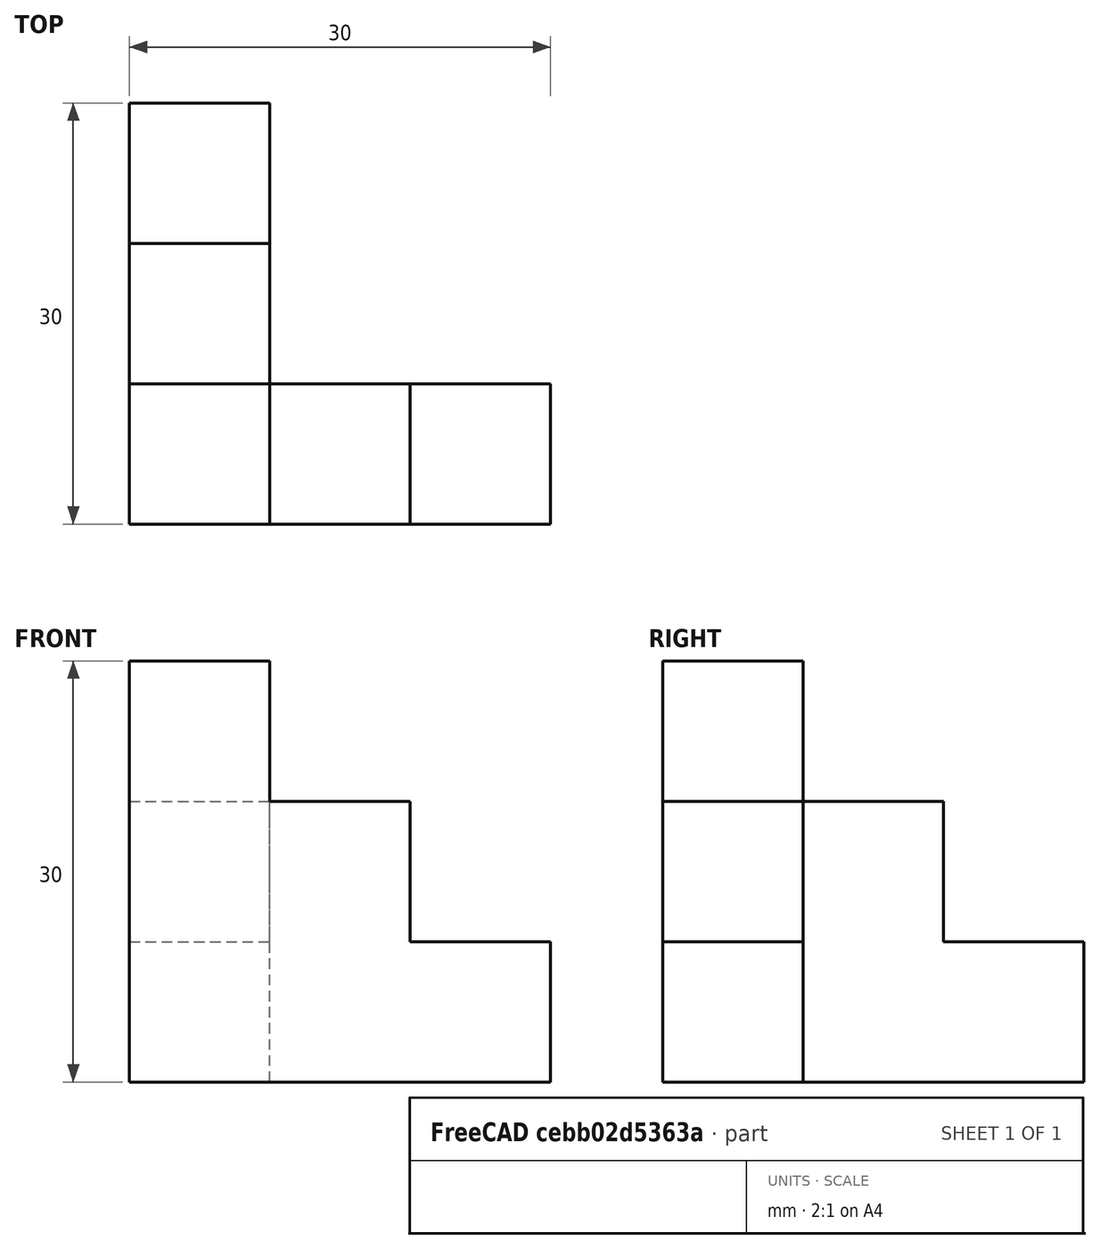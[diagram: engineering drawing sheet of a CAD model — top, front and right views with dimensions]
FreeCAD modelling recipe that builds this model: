
FCSTD DOCUMENT  (FreeCAD 0.21R33771 (Git))
Label: OJT1_T05R02_unions_qubert3_v2
License: All rights reserved
LicenseURL: http://en.wikipedia.org/wiki/All_rights_reserved
objects: Part::Box×5, Part::MultiFuse×1
note: 6 computed .brp shape members not serialized (recipe doc carries the construction recipe); baked Part::Feature solids carry a one-line shape summary decoded from their .brp

FEATURE [Part::Box] Box  label="nivell1_cub1"
  AttacherType = Attacher::AttachEngine3D
  Height = 30
  Length = 10
  Width = 10
FEATURE [Part::Box] Box001  label="nivell1_cub2"
  AttacherType = Attacher::AttachEngine3D
  Height = 20
  Length = 10
  Placement = pos=(10,0,0) rot=(0,0,1;0rad)
  Width = 10
FEATURE [Part::Box] Box002  label="nivell1_cub3"
  AttacherType = Attacher::AttachEngine3D
  Height = 20
  Length = 10
  Placement = pos=(0,10,0) rot=(0,0,1;0rad)
  Width = 10
FEATURE [Part::Box] Box003  label="nivell1_cub4"
  AttacherType = Attacher::AttachEngine3D
  Height = 10
  Length = 10
  Placement = pos=(20,0,0) rot=(0,0,1;0rad)
  Width = 10
FEATURE [Part::Box] Box004  label="nivell1_cub5"
  AttacherType = Attacher::AttachEngine3D
  Height = 10
  Length = 10
  Placement = pos=(0,20,0) rot=(0,0,1;0rad)
  Width = 10
FEATURE [Part::MultiFuse] Fusion  label="qubert_3"
  Refine = true
  Shapes = -> [Box004,Box,Box001,Box002,Box003]
